# Revit family: Chair-Soft_Seating-Allermuir-Stirling-SL03
name_source: partatom
category: Furniture
revit_build: Autodesk Revit MEP 2012 (Build: 20110916_2132)
units: mm (PartAtom-declared; Revit-internal decimal feet)

## types (1)
- SL03
    04 CSI = 12 51 00
    95 CSI = 12510
    Arms Height = 25 77/128"
    Assembly Code = E2020200
    Base = Metal - Allermuir - Polished Aluminum
    Brochure URL = http://www.allermuir.net
    CAD Blocks URL = http://www.allermuir.net
    Color Availability = See price list for material options
    Default Elevation = 48"
    Description = Three seater with narrow arms
    Fabric Spec Sheets = http://www.allermuir.net
    Manufacturer = Allermuir
    Manufacturer Fax = (419) 887 5805
    Model = SL03
    Overall Depth = 36 51/256"
    Overall Height = 35"
    Overall Width = 100"
    Plastic Arms in Black = No
    Plastic glides = Yes
    Plugin Data URL = http://products.ecoscorecard.com
    Pricing URL = http://www.allermuir.net
    Product Line = Stirling
    Product Page URL = http://www.allermuir.net
    Seat Depth = 23 1/2"
    Seat Height = 18"
    Seat Width = 88 51/256"
    Seat or Top = Fabric - Allermuir - Silcoates
    Specifications URL = http://www.allermuir.net
    Stacks = No
    Subcategory = Soft Seating
    Tubular Steel Legs = No
    URL = http://www.allermuir.net
    Upholstered Back = Yes
    Upholstered Seat = Yes
    Weight = 328.00 lb
    ecoScorecard Product Page = http://products.ecoscorecard.com
    ecoScorecard_data = http://thesenatorgroup.ecoscorecard.com

## geometry (parser evidence)
native form markers: Blend x34, Sweep x4
no freeform markers — native parametric forms only
